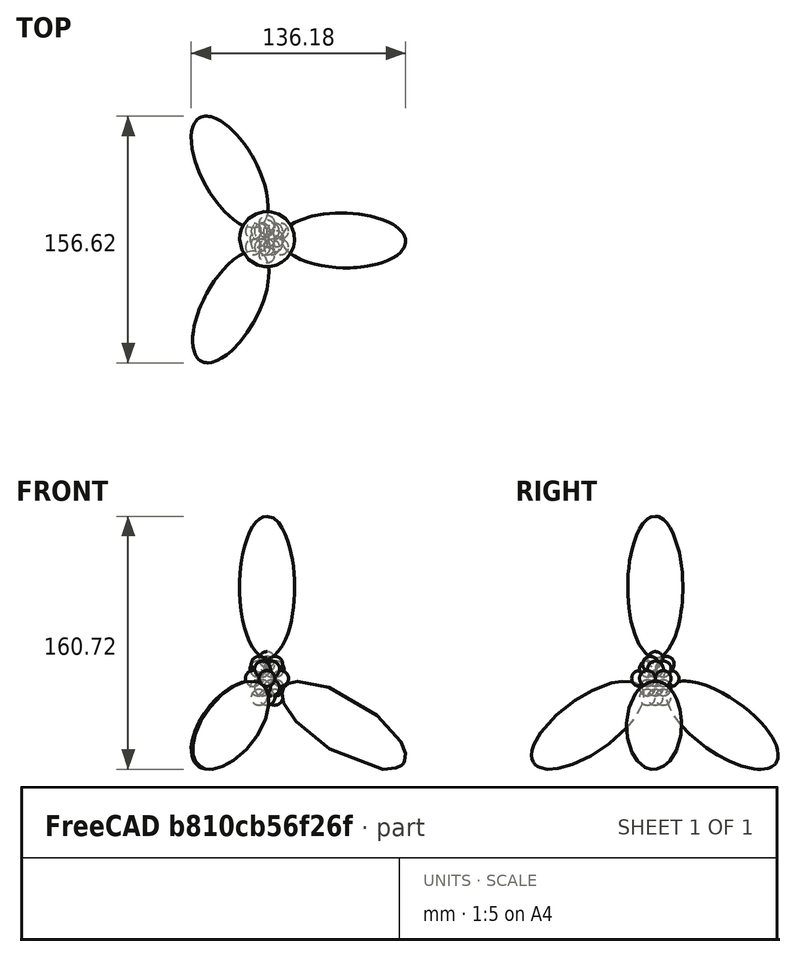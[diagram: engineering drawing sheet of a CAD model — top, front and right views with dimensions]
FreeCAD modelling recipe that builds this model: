
FCSTD DOCUMENT  (FreeCAD 1.1R43510 (Git))
Label: 02-si-atom
License: All rights reserved
LicenseURL: http://en.wikipedia.org/wiki/All_rights_reserved
objects: Part::Feature×23, Part::Part2DObjectPython×14, Part::Sphere×9, App::DocumentObjectGroup×5, Sketcher::SketchObject×1, PartDesign::Revolution×1
note: 51 computed .brp shape members not serialized (recipe doc carries the construction recipe); baked Part::Feature solids carry a one-line shape summary decoded from their .brp

FEATURE [Part::Feature] Sphere001
  Placement = pos=(0,-10,31) rot=(0,0,1;0rad)
  shape: bbox 10 x 10 x 10 mm, 1 faces (baked)
FEATURE [Part::Feature] Sphere002
  Placement = pos=(-8.66025,-5,31) rot=(0,0,1;0rad)
  shape: bbox 10 x 10 x 10 mm, 1 faces (baked)
FEATURE [Part::Feature] Sphere003
  Placement = pos=(-8.66025,5,31) rot=(0,0,1;0rad)
  shape: bbox 10 x 10 x 10 mm, 1 faces (baked)
FEATURE [Part::Feature] Sphere004
  Placement = pos=(8.66025,-5,31) rot=(0,0,1;0rad)
  shape: bbox 10 x 10 x 10 mm, 1 faces (baked)
FEATURE [Part::Feature] Sphere005
  Placement = pos=(8.66025,5,31) rot=(0,0,1;0rad)
  shape: bbox 10 x 10 x 10 mm, 1 faces (baked)
FEATURE [Part::Feature] Sphere006
  Placement = pos=(4e-12,10,31) rot=(0,0,1;0rad)
  shape: bbox 10 x 10 x 10 mm, 1 faces (baked)
FEATURE [Part::Sphere] Sphere007
  Angle1 = -90
  Angle2 = 90
  Angle3 = 360
  AttacherType = Attacher::AttachEngine3D
  Placement = pos=(0,0,31) rot=(0,0,1;0rad)
  Radius = 5
FEATURE [Part::Feature] Sphere  label="Sphere027"
  Placement = pos=(-3,5,37) rot=(0,0,1;0rad)
  shape: bbox 10 x 10 x 10 mm, 1 faces (baked)
FEATURE [Part::Feature] Sphere008  label="Sphere028"
  Placement = pos=(2.83013,5.09808,37) rot=(0,0,1;0rad)
  shape: bbox 10 x 10 x 10 mm, 1 faces (baked)
FEATURE [Part::Feature] Sphere009  label="Sphere029"
  Placement = pos=(5.83013,0.0980762,37) rot=(0,0,1;0rad)
  shape: bbox 10 x 10 x 10 mm, 1 faces (baked)
FEATURE [Part::Feature] Sphere010  label="Sphere030"
  Placement = pos=(3,-5,37) rot=(0,0,1;0rad)
  shape: bbox 10 x 10 x 10 mm, 1 faces (baked)
FEATURE [Part::Feature] Sphere011  label="Sphere031"
  Placement = pos=(-2.83013,-5.09808,37) rot=(0,0,1;0rad)
  shape: bbox 10 x 10 x 10 mm, 1 faces (baked)
FEATURE [Part::Feature] Sphere012  label="Sphere032"
  Placement = pos=(-5.83013,-0.0980762,37) rot=(0,0,1;0rad)
  shape: bbox 10 x 10 x 10 mm, 1 faces (baked)
FEATURE [Part::Feature] Sphere013  label="Sphere033"
  Placement = pos=(-3,5,25) rot=(0,0,1;0rad)
  shape: bbox 10 x 10 x 10 mm, 1 faces (baked)
FEATURE [Part::Feature] Sphere014  label="Sphere034"
  Placement = pos=(2.83013,5.09808,25) rot=(0,0,1;0rad)
  shape: bbox 10 x 10 x 10 mm, 1 faces (baked)
FEATURE [Part::Feature] Sphere015  label="Sphere035"
  Placement = pos=(-2.83013,-5.09808,25) rot=(0,0,1;0rad)
  shape: bbox 10 x 10 x 10 mm, 1 faces (baked)
FEATURE [Part::Feature] Sphere016  label="Sphere036"
  Placement = pos=(5.83013,0.0980762,25) rot=(0,0,1;0rad)
  shape: bbox 10 x 10 x 10 mm, 1 faces (baked)
FEATURE [Part::Feature] Sphere017  label="Sphere015"
  Placement = pos=(3,-5,25) rot=(0,0,1;0rad)
  shape: bbox 10 x 10 x 10 mm, 1 faces (baked)
FEATURE [Part::Feature] Sphere018  label="Sphere037"
  Placement = pos=(-5.83013,-0.0980762,25) rot=(0,0,1;0rad)
  shape: bbox 10 x 10 x 10 mm, 1 faces (baked)
FEATURE [Part::Sphere] Sphere019
  Angle1 = -90
  Angle2 = 90
  Angle3 = 360
  AttacherType = Attacher::AttachEngine3D
  Placement = pos=(0,0,43) rot=(0,0,1;0rad)
  Radius = 5
FEATURE [Part::Sphere] Sphere020  label="Sphere038"
  Angle1 = -90
  Angle2 = 90
  Angle3 = 360
  AttacherType = Attacher::AttachEngine3D
  Placement = pos=(0,0,19) rot=(0,0,1;0rad)
  Radius = 5
FEATURE [Part::Sphere] Sphere021  label="Sphere039"
  Angle1 = -90
  Angle2 = 90
  Angle3 = 360
  AttacherType = Attacher::AttachEngine3D
  Placement = pos=(0,7,40) rot=(0,0,1;0rad)
  Radius = 5
FEATURE [Part::Sphere] Sphere022  label="Sphere040"
  Angle1 = -90
  Angle2 = 90
  Angle3 = 360
  AttacherType = Attacher::AttachEngine3D
  Placement = pos=(-5,-3,40) rot=(0,0,1;0rad)
  Radius = 5
FEATURE [Part::Sphere] Sphere023  label="Sphere041"
  Angle1 = -90
  Angle2 = 90
  Angle3 = 360
  AttacherType = Attacher::AttachEngine3D
  Placement = pos=(5,-3,40) rot=(0,0,1;0rad)
  Radius = 5
FEATURE [Part::Sphere] Sphere024  label="Sphere042"
  Angle1 = -90
  Angle2 = 90
  Angle3 = 360
  AttacherType = Attacher::AttachEngine3D
  Placement = pos=(-5,5,19) rot=(0,0,1;0rad)
  Radius = 5
FEATURE [Part::Sphere] Sphere025  label="Sphere043"
  Angle1 = -90
  Angle2 = 90
  Angle3 = 360
  AttacherType = Attacher::AttachEngine3D
  Placement = pos=(5,5,19) rot=(0,0,1;0rad)
  Radius = 5
FEATURE [Part::Sphere] Sphere026  label="Sphere044"
  Angle1 = -90
  Angle2 = 90
  Angle3 = 360
  AttacherType = Attacher::AttachEngine3D
  Placement = pos=(0,-5,19) rot=(0,0,1;0rad)
  Radius = 5
FEATURE [App::DocumentObjectGroup] Group  label="core"
  Group = -> [Sphere001,Sphere002,Sphere003,Sphere004,Sphere005,Sphere006,Sphere007,Sphere,Sphere008,Sphere009,Sphere010,Sphere011,Sphere012,Sphere013,Sphere014,Sphere015,Sphere016,Sphere017,Sphere018,Sphere019,Sphere020,Sphere021,Sphere022,Sphere023,Sphere024,Sphere025,Sphere026]
FEATURE [Part::Part2DObjectPython] Polygon  # Draft 2D object (typed FeaturePython)
  ChamferSize = 0
  DrawMode = 0
  FacesNumber = 3
  FilletRadius = 0
  MakeFace = false
  MapMode = 5
  Radius = 50
FEATURE [Part::Part2DObjectPython] Line  # Draft 2D object (typed FeaturePython)
  ChamferSize = 0
  Closed = false
  End = (0.452401,-0.175885,80)
  FilletRadius = 0
  Length = 80
  MakeFace = true
  MapMode = 5
  Points = (2) [(0.452401,-0.175885,0),(0.452401,-0.175885,80)]
  Start = (0.452401,-0.175885,0)
  Subdivisions = 0
FEATURE [Part::Part2DObjectPython] Arc  # Draft 2D object (typed FeaturePython)
  FirstAngle = -171.133
  LastAngle = -90
  MakeFace = true
  MapMode = 5
  Placement = pos=(-25,43.3013,0) rot=(0,0,1;0rad)
  Radius = 86.6025
FEATURE [Part::Part2DObjectPython] Arc001  # Draft 2D object (typed FeaturePython)
  FirstAngle = 90
  LastAngle = 169.455
  MakeFace = true
  MapMode = 5
  Placement = pos=(-25,-43.3013,0) rot=(0,0,1;0rad)
  Radius = 86.6025
FEATURE [Part::Part2DObjectPython] Line001  # Draft 2D object (typed FeaturePython)
  ChamferSize = 0
  Closed = false
  End = (-25,0,0)
  FilletRadius = 0
  Length = 75
  MakeFace = true
  MapMode = 5
  Points = (2) [(-100,0,0),(-25,-2.13163e-14,0)]
  Start = (-100,0,0)
  Subdivisions = 0
FEATURE [Part::Part2DObjectPython] Arc002  # Draft 2D object (typed FeaturePython)
  FirstAngle = 52.9075
  LastAngle = 180
  MakeFace = true
  MapMode = 5
  Placement = pos=(-25,0,0) rot=(1,0,0;1.5708rad)
  Radius = 75
FEATURE [Part::Part2DObjectPython] Line002  # Draft 2D object (typed FeaturePython)
  ChamferSize = 0
  Closed = false
  End = (-25,-43.3013,0)
  FilletRadius = 0
  Length = 87.0816
  MakeFace = true
  MapMode = 5
  Points = (2) [(1.07885,0,70.9091),(-25,-43.3013,0)]
  Start = (1.07885,0,70.9091)
  Subdivisions = 0
FEATURE [Part::Part2DObjectPython] Line003  # Draft 2D object (typed FeaturePython)
  ChamferSize = 0
  Closed = false
  End = (50,0,0)
  FilletRadius = 0
  Length = 86.1474
  MakeFace = true
  MapMode = 5
  Points = (2) [(1.07885,0,70.9091),(50,1.53081e-15,0)]
  Start = (1.07885,0,70.9091)
  Subdivisions = 0
FEATURE [Part::Part2DObjectPython] Line004  # Draft 2D object (typed FeaturePython)
  ChamferSize = 0
  Closed = false
  End = (-25,43.3013,0)
  FilletRadius = 0
  Length = 87.0816
  MakeFace = true
  MapMode = 5
  Points = (2) [(1.07885,0,70.9091),(-25,43.3013,0)]
  Start = (1.07885,0,70.9091)
  Subdivisions = 0
FEATURE [App::DocumentObjectGroup] Group001  label="tetrahedron"
  Group = -> [Line002,Line003,Line004,Polygon]
FEATURE [Part::Part2DObjectPython] Line006  # Draft 2D object (typed FeaturePython)
  ChamferSize = 0
  Closed = false
  End = (50,0,0)
  FilletRadius = 0
  Length = 58.8303
  MakeFace = true
  MapMode = 5
  Points = (2) [(0,0,31),(50,1.53081e-15,0)]
  Start = (0,0,31)
  Subdivisions = 0
FEATURE [Part::Part2DObjectPython] Line007  # Draft 2D object (typed FeaturePython)
  ChamferSize = 0
  Closed = false
  End = (1.07885,0,70.9091)
  FilletRadius = 0
  Length = 39.9237
  MakeFace = true
  MapMode = 5
  Points = (2) [(0,0,31),(1.07885,0,70.9091)]
  Start = (0,0,31)
  Subdivisions = 0
FEATURE [Part::Part2DObjectPython] Line008  # Draft 2D object (typed FeaturePython)
  ChamferSize = 0
  Closed = false
  End = (-25,43.3013,0)
  FilletRadius = 0
  Length = 58.8303
  MakeFace = true
  MapMode = 5
  Points = (2) [(0,0,31),(-25,43.3013,0)]
  Start = (0,0,31)
  Subdivisions = 0
FEATURE [Sketcher::SketchObject] Sketch
  ArcFitTolerance = 0
  ExternalTypes = [0]
  FullyConstrained = true
  MakeInternals = false
  MapMode = 5
  Placement = pos=(0,0,0) rot=(1,0,0;1.5708rad)
  sketch-geometry (6):
    g0: LineSegment StartX=0 StartY=60 StartZ=0 EndX=-1.18951e-11 EndY=150 EndZ=0
    g1: ArcOfEllipse CenterX=0 CenterY=105 CenterZ=0 NormalX=0 NormalY=0 NormalZ=1 MajorRadius=45 MinorRadius=17.5 AngleXU=1.5708 StartAngle=3.14159 EndAngle=6.28319
    g2: LineSegment [constr] StartX=-1.18951e-11 StartY=150 StartZ=0 EndX=0 EndY=60 EndZ=0
    g3: LineSegment [constr] StartX=-17.5 StartY=105 StartZ=0 EndX=17.5 EndY=105 EndZ=0
    g4: GeomPoint [constr] X=-4.2898e-12 Y=146.458 Z=0
    g5: GeomPoint [constr] X=0 Y=63.5422 Z=0
  constraints (10):
    c: PointOnObject(g0,g-2)
    c: PointOnObject(g0,g-2)
    c: InternalAlignment(g2-g5 -> g1) x4
    c: Coincident(g2,g0)
    c: Coincident(g1,g0)
    c: Coincident(g2,g0)
    c: DistanceX(g3,g3) = 35
    c: DistanceY(g-1,g0) = 60
    c: DistanceY(g0,g0) = 90
    c: Coincident(g1,g0)
FEATURE [PartDesign::Revolution] Revolution001  label="orbital-1"
  AllowMultiFace = false
  Angle = 360
  Angle2 = 60
  Axis = (0,0,1)
  Base = (0,0,0)
  Placement = pos=(0,0,0) rot=(1,0,0;1.5708rad)
  Profile = -> Sketch
  ReferenceAxis = -> Sketch [V_Axis]
  Refine = true
  Reversed = true
  Suppressed = false
  Type = 0
FEATURE [Part::Feature] Face
  shape: bbox 40.2 x 69.18 x 91.71 mm, 1 faces, 0 solids (baked)
FEATURE [Part::Part2DObjectPython] Arc003  # Draft 2D object (typed FeaturePython)
  FirstAngle = -223.482
  LastAngle = -86.8237
  MakeFace = true
  MapMode = 5
  Placement = pos=(0,0,31) rot=(-0.761669,-0.469136,0.446958;1.79277rad)
  Radius = 39.9237
FEATURE [Part::Part2DObjectPython] Line010  # Draft 2D object (typed FeaturePython)
  ChamferSize = 0
  Closed = false
  End = (68.0246,117.822,115.351)
  FilletRadius = 0
  Length = 200
  MakeFace = true
  MapMode = 5
  Points = (2) [(-16.9656,-29.3853,9.96263),(68.0246,117.822,115.351)]
  Start = (-16.9656,-29.3853,9.96263)
  Subdivisions = 0
FEATURE [App::DocumentObjectGroup] Group002  label="Aux"
  Group = -> [Line,Arc,Arc001,Line001,Arc002,Line006,Line007,Line008,Face,Arc003,Line010]
FEATURE [App::DocumentObjectGroup] Group003  label="Orbital-src"
  Group = -> [Revolution001]
FEATURE [Part::Feature] Revolution001001  label="orbital-005"
  Placement = pos=(0,0,-16) rot=(1,0,0;1.5708rad)
  shape: bbox 35 x 35 x 90 mm, 1 faces (baked)
FEATURE [Part::Feature] Clone003  label="orbital-006"
  Placement = pos=(-65.4544,-121.45,-54.0897) rot=(0.801351,0.44296,-0.402024;0.815302rad)
  shape: bbox 48.41 x 71.09 x 55.95 mm, 1 faces (baked)
FEATURE [Part::Feature] Clone004  label="orbital-007"
  Placement = pos=(137.942,-2.53521,-54.0897) rot=(0.019523,0.459459,0.887984;1.81952rad)
  shape: bbox 78.57 x 34.89 x 55.95 mm, 1 faces (baked)
FEATURE [Part::Feature] Clone005  label="orbital-008"
  Placement = pos=(-66.7753,120.729,-54.0897) rot=(-0.321183,0.204089,0.924764;3.75111rad)
  shape: bbox 48.78 x 70.87 x 55.95 mm, 1 faces (baked)
FEATURE [App::DocumentObjectGroup] Group004  label="Orbitales"
  Group = -> [Revolution001001,Clone003,Clone004,Clone005]
